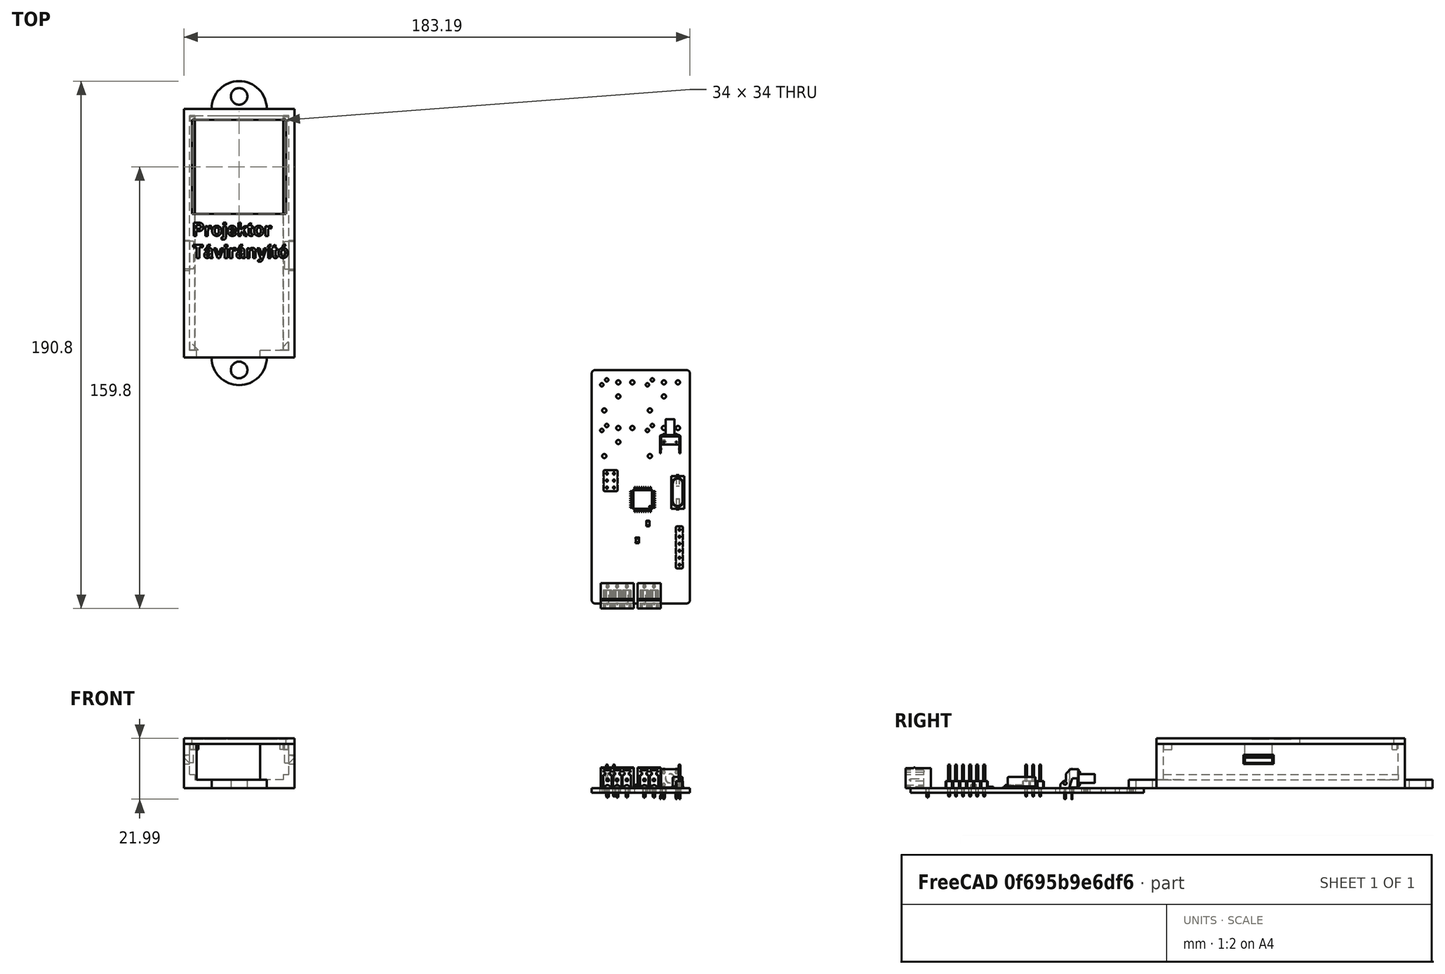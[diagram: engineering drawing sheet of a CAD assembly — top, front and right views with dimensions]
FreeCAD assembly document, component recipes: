
FREECAD ASSEMBLY — COMPONENT RECIPES ("doboz_v4")

This assembly document has 2 components, labeled P0..P1 below (a component is one placed body or linked part). 1 of them carries a construction recipe — the FreeCAD feature program that regenerates the part from scratch, quoted from this document or its linked companion documents; the rest are supplied as boundary geometry only. No exploded tour is included for this assembly.
COMPONENT P0 — geometry summary ("SEM_ProjektoroSCH-Rev2"; no construction recipe available for this part):
  bounding box: 86.3 x 35.6 x 12.5 mm
  tessellated surface: 117,506 triangles
  volume: 6876 mm^3 (18% of its bounding box)
COMPONENT P1 — recipe-attached ("Body", modeled in this document).
Construction recipe (the document's own serialized feature program — sketch geometry with constraints, then the solid features built on it; lengths are millimeters unless a unit is written):

FEATURE [Sketcher::SketchObject] Sketch
  FullyConstrained = true
  MapMode = 5
  Support = -> [XY_Plane004]
  sketch-geometry (4):
    g0: LineSegment StartX=-20 StartY=45 StartZ=0 EndX=20 EndY=45 EndZ=0
    g1: LineSegment StartX=20 StartY=45 StartZ=0 EndX=20 EndY=-45 EndZ=0
    g2: LineSegment StartX=20 StartY=-45 StartZ=0 EndX=-20 EndY=-45 EndZ=0
    g3: LineSegment StartX=-20 StartY=-45 StartZ=0 EndX=-20 EndY=45 EndZ=0
  constraints (11):
    c: Coincident(g0,g1)
    c: Coincident(g1,g2)
    c: Coincident(g2,g3)
    c: Coincident(g3,g0)
    c: Horizontal(g0)
    c: Horizontal(g2)
    c: Vertical(g1)
    c: Vertical(g3)
    c: Symmetric(g2,g0,g-1)
    c: DistanceX(g0,g0) = 40
    c: DistanceY(g1,g1) = 90
FEATURE [PartDesign::Pad] Pad
  Direction = (0,0,1)
  Length = 16
  Length2 = 10
  Profile = -> Sketch
  ReferenceAxis = -> Sketch [N_Axis]
  Type = 0
FEATURE [Sketcher::SketchObject] Sketch001
  FullyConstrained = true
  MapMode = 5
  Placement = pos=(0,0,16) rot=(0,0,1;0rad)
  Support = -> [Pad]
  sketch-geometry (4):
    g0: LineSegment StartX=-16 StartY=42.5 StartZ=0 EndX=16 EndY=42.5 EndZ=0
    g1: LineSegment StartX=16 StartY=42.5 StartZ=0 EndX=16 EndY=-42.5 EndZ=0
    g2: LineSegment StartX=16 StartY=-42.5 StartZ=0 EndX=-16 EndY=-42.5 EndZ=0
    g3: LineSegment StartX=-16 StartY=-42.5 StartZ=0 EndX=-16 EndY=42.5 EndZ=0
  constraints (11):
    c: Coincident(g0,g1)
    c: Coincident(g1,g2)
    c: Coincident(g2,g3)
    c: Coincident(g3,g0)
    c: Horizontal(g0)
    c: Horizontal(g2)
    c: Vertical(g1)
    c: Vertical(g3)
    c: Symmetric(g2,g0,g-1)
    c: DistanceX(g0,g0) = 32
    c: DistanceY(g1,g1) = 85
FEATURE [PartDesign::Pocket] Pocket
  BaseFeature = -> Pad
  Direction = (0,0,-1)
  Length = 13
  Length2 = 5
  Profile = -> Sketch001
  ReferenceAxis = -> Sketch001 [N_Axis]
  Type = 0
FEATURE [PartDesign::Body] Body
  Group = -> [Sketch,Pad,Sketch001,Pocket]
  Origin = -> Origin004
  Tip = -> Pocket
PROVENANCE & LICENSES
A FreeCAD (.FCStd) document from a public repository crawl; recipes are the document's own serialized feature recipes (and, for linked parts, companion documents' recipes).
License: mit.
